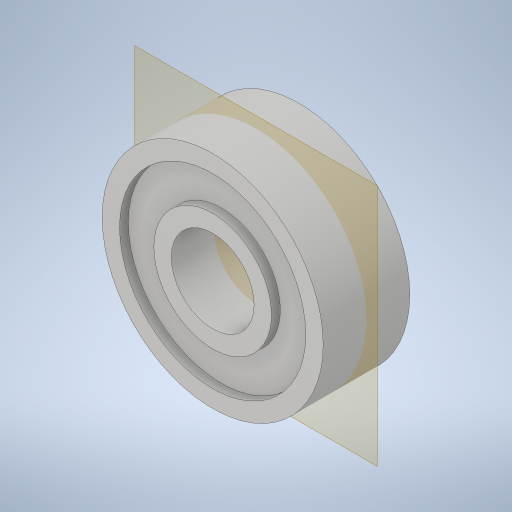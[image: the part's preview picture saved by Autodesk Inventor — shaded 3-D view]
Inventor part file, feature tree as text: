
AUTODESK INVENTOR PART (.ipt)
format: ipt  version: 2023.3 (Build 273359000, 359)  size: 281,600 bytes
history: native  units: in
note: dims shown in document units (in); Inventor stores cm internally (conversion verified against a paired STEP export)
features: plane x1, revolve x1
ambient origin geometry x8: Origin, YZ Plane, XZ Plane, XY Plane, X Axis, Y Axis, Z Axis, Center Point
bodies: Solid1 (feature_tree)
feature tree (2):
  plane  "Work Plane1"
  revolve  "Revolve1"  [1 undecoded]
note: 1 required parameter value undecoded (feature->parameter linkage not recoverable at this tier; creation-order binding heuristic only, values carry confidence <= 0.55)
